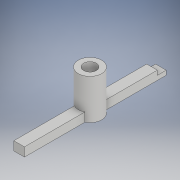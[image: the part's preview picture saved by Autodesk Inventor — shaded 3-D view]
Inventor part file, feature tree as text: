
AUTODESK INVENTOR PART (.ipt)
format: ipt  version: 2019 (Build 230136000, 136)  size: 158,720 bytes
history: native  units: in
note: dims shown in document units (in); Inventor stores cm internally (conversion verified against a paired STEP export)
features: extrude x6, sketch x6, projected_geometry x3
ambient origin geometry x8: Origin, YZ Plane, XZ Plane, XY Plane, X Axis, Y Axis, Z Axis, Center Point
bodies: Solid1 (feature_tree)
feature tree (15):
  extrude  "Extrusion1"  Depth=0.36in
  extrude  "Extrusion2"  Depth=0.1in TaperAngle=0.0deg
  extrude  "Extrusion7"  TaperAngle=0.0deg  [1 undecoded]
  extrude  "Extrusion18"  TaperAngle=0.0deg  [1 undecoded]
  extrude  "Extrusion19"  Depth=4.0in
  extrude  "Extrusion20"  Depth=0.25in
  sketch  "Sketch1"  dims[d0=0.36in d1=0.15in]
  sketch  "Sketch2"  dims[d2=0.78in d3=0.0in d4=0.1in d5=0.0in]
  sketch  "Sketch10"  dims[d28=0.875in d29=0.0in d42=0.0in]
  sketch  "Sketch24"  dims[d43=0.0in d44=0.0in]
  projected_geometry  "Projected Loop15"
  sketch  "Sketch25"  dims[d90=4.0in d91=2.0in]
  projected_geometry  "Projected Loop16"
  projected_geometry  "Projected Loop17"
  sketch  "Sketch26"  dims[d92=0.15in d93=0.15in d94=0.25in d95=0.0in d96=0.25in d97=0.0in d98=0.125in d99=0.25in d100=1.0in d101=0.0in]
note: 2 required parameter values undecoded (feature->parameter linkage not recoverable at this tier; creation-order binding heuristic only, values carry confidence <= 0.55)
